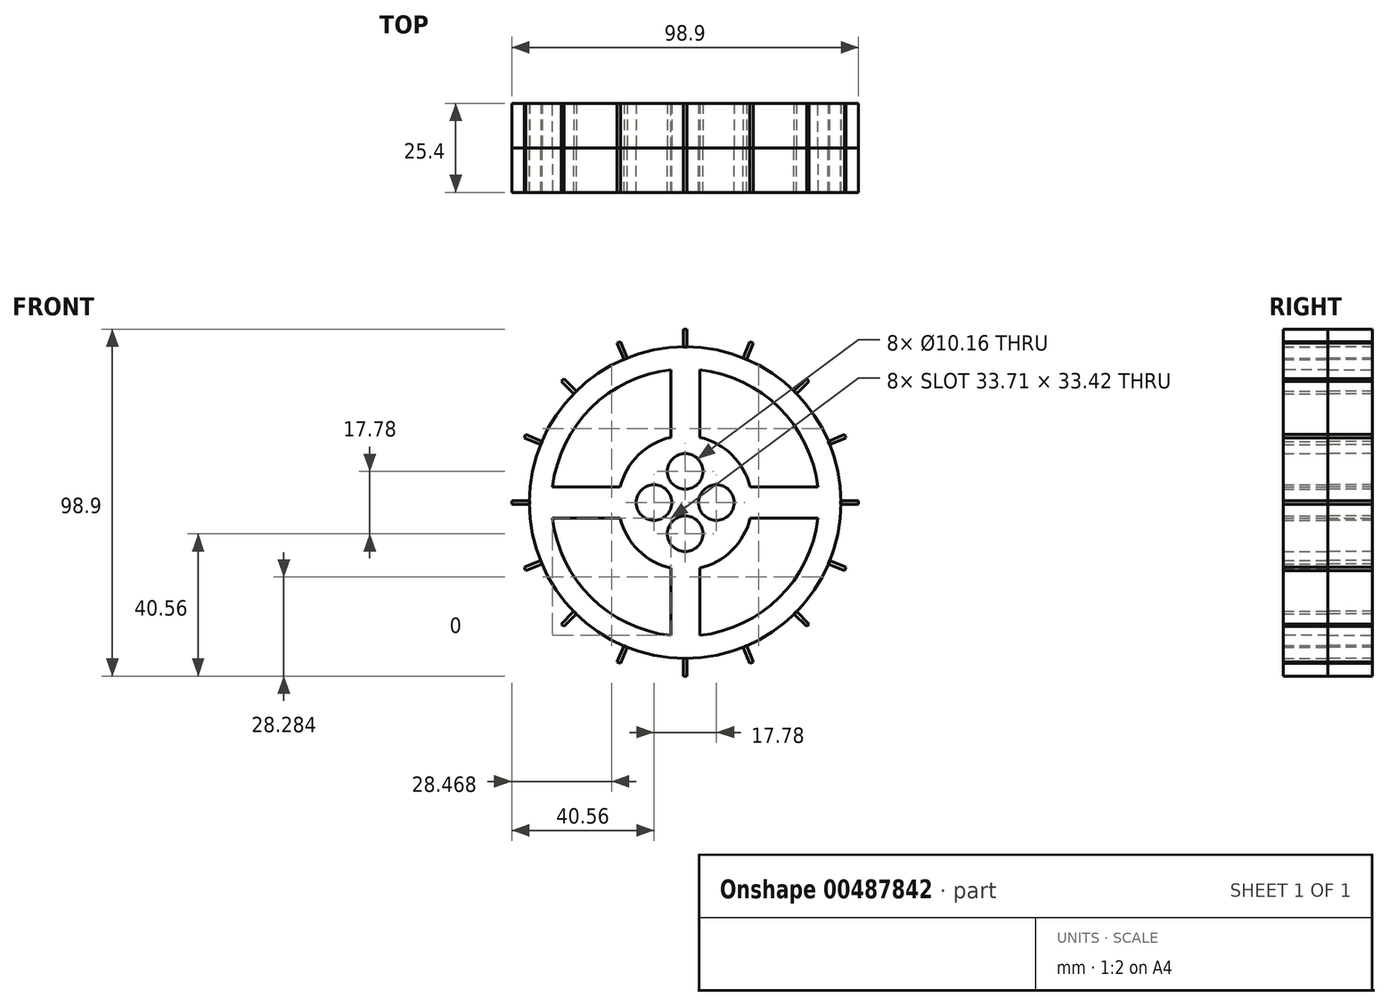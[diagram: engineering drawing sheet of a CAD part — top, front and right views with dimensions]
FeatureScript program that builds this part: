
annotation { "Feature Type Name" : "Feature", "Feature Type Description" : "" }
export const myFeature = defineFeature(function(context is Context, id is Id, definition is map)
    precondition{}
    {
        {
            var Q0;
            Q0=qCreatedBy(makeId("Front.planeOp"),FACE);
            var sketch = newSketch(context, id + "F0", { "sketchPlane" : qUnion([Q0])});
            skCircle(sketch, "E0", {"center": v(0, 0) * mm, "radius": 44.45 * mm});
            skSolve(sketch);
        }
        {
            var Q0;
            Q0=makeQuery(id+"F0.imprint","IMPRINT",FACE,{"disambiguationData":[TD([[makeQuery(id+"F0.imprint","IMPRINT",EDGE,{"derivedFrom":sQuery(id+"F0.wireOp",EDGE,"E0")}),1.0]])]});
            extrude(context, id + "F1", {"entities" : qUnion([Q0]), "depth" : 12.7 * mm});
        }
        {
            var Q0;
            Q0=makeQuery(id+"F1.opExtrude","CAP_FACE",FACE,{"disambiguationData":[OSD([sQuery(id+"F0.wireOp",EDGE,"E0")])],"isStart":false});
            var sketch = newSketch(context, id + "F2", { "sketchPlane" : qUnion([Q0])});
            skCircle(sketch, "E1", {"center": v(0, 0) * mm, "radius": 50.8 * mm});
            skSolve(sketch);
        }
        {
            var Q0;
            Q0=sQuery(id+"F2.wireOp",VERTEX,"E1.center");
            var Q1;
            Q1=makeQuery(id+"F1.opExtrude","SWEPT_BODY",BODY,{"disambiguationData":[OSD([sQuery(id+"F0.wireOp",EDGE,"E0")])]});
            hole(context, id + "F3", {"style" : HoleStyle.SIMPLE, "endStyle" : HoleEndStyle.THROUGH, "holeDiameter" : 76.2 * mm, "isTappedThrough" : true, "tappedDepth" : 12.7 * mm, "tapClearance" : 3, "locations" : qUnion([Q0]), "scope" : qUnion([Q1])});
        }
        {
            var Q0;
            Q0=qCreatedBy(makeId("Front.planeOp"),FACE);
            var sketch = newSketch(context, id + "F4", { "sketchPlane" : qUnion([Q0])});
            skLineSegment(sketch, "E2.bottom", {"start": v(4.13, -42.15) * mm, "end": v(-4.13, -42.15) * mm});
            skLineSegment(sketch, "E2.top", {"start": v(4.13, 42.15) * mm, "end": v(-4.13, 42.15) * mm});
            skLineSegment(sketch, "E2.left", {"start": v(4.13, -42.15) * mm, "end": v(4.13, 42.15) * mm});
            skLineSegment(sketch, "E2.right", {"start": v(-4.13, -42.15) * mm, "end": v(-4.13, 42.15) * mm});
            skPoint(sketch, "E2.middle", {"position": v(0, 0) * mm});
            skLineSegment(sketch, "E3.bottom", {"start": v(42.66, 4.46) * mm, "end": v(-42.66, 4.46) * mm});
            skLineSegment(sketch, "E3.top", {"start": v(42.66, -4.46) * mm, "end": v(-42.66, -4.46) * mm});
            skLineSegment(sketch, "E3.left", {"start": v(42.66, 4.46) * mm, "end": v(42.66, -4.46) * mm});
            skLineSegment(sketch, "E3.right", {"start": v(-42.66, 4.46) * mm, "end": v(-42.66, -4.46) * mm});
            skSolve(sketch);
        }
        {
            var Q0;
            {var subQ5=sQuery(id+"F4.wireOp",EDGE,"E3.left");Q0=makeQuery(id+"F4.imprint","IMPRINT",FACE,{"disambiguationData":[TD([[makeQuery(id+"F4.imprint","IMPRINT",EDGE,{"derivedFrom":subQ5}),-1.0]])]});}
            var Q1;
            {var subQ5=sQuery(id+"F4.wireOp",EDGE,"E3.right");Q1=makeQuery(id+"F4.imprint","IMPRINT",FACE,{"disambiguationData":[TD([[makeQuery(id+"F4.imprint","IMPRINT",EDGE,{"derivedFrom":subQ5}),1.0]])]});}
            var Q2;
            {var subQ0=sQuery(id+"F4.wireOp",EDGE,"E3.top");var subQ1=sQuery(id+"F4.wireOp",EDGE,"E2.left");var subQ2=makeQuery(id+"F4.imprint","INTERSECT",VERTEX,{"derivedFrom":[subQ1,subQ0]});Q2=makeQuery(id+"F4.imprint","IMPRINT",FACE,{"disambiguationData":[TD([[makeQuery(id+"F4.imprint","IMPRINT",EDGE,{"disambiguationData":[TD([[subQ2,-1.0]])],"derivedFrom":subQ1}),1.0]])]});}
            var Q3;
            {var subQ0=sQuery(id+"F4.wireOp",EDGE,"E2.top");Q3=makeQuery(id+"F4.imprint","IMPRINT",FACE,{"disambiguationData":[TD([[makeQuery(id+"F4.imprint","IMPRINT",EDGE,{"derivedFrom":subQ0}),1.0]])]});}
            var Q4;
            {var subQ0=sQuery(id+"F4.wireOp",EDGE,"E2.bottom");Q4=makeQuery(id+"F4.imprint","IMPRINT",FACE,{"disambiguationData":[TD([[makeQuery(id+"F4.imprint","IMPRINT",EDGE,{"derivedFrom":subQ0}),-1.0]])]});}
            extrude(context, id + "F5", {"entities" : qUnion([Q0, Q1, Q2, Q3, Q4]), "operationType" : NewBodyOperationType.ADD, "depth" : 12.7 * mm});
        }
        {
            var Q0;
            Q0=qCreatedBy(makeId("Front.planeOp"),FACE);
            var sketch = newSketch(context, id + "F6", { "sketchPlane" : qUnion([Q0])});
            skCircle(sketch, "E4", {"center": v(0, 0) * mm, "radius": 19.05 * mm});
            skSolve(sketch);
        }
        {
            var Q0;
            Q0=makeQuery(id+"F6.imprint","IMPRINT",FACE,{"disambiguationData":[TD([[makeQuery(id+"F6.imprint","IMPRINT",EDGE,{"derivedFrom":sQuery(id+"F6.wireOp",EDGE,"E4")}),1.0]])]});
            extrude(context, id + "F7", {"entities" : qUnion([Q0]), "operationType" : NewBodyOperationType.ADD, "depth" : 12.7 * mm});
        }
        {
            var Q0;
            Q0=qCreatedBy(makeId("Front.planeOp"),FACE);
            var sketch = newSketch(context, id + "F8", { "sketchPlane" : qUnion([Q0])});
            skCircle(sketch, "E5", {"center": v(0, 8.9) * mm, "radius": 5.08 * mm});
            skCircle(sketch, "E6", {"center": v(8.9, 0) * mm, "radius": 5.08 * mm});
            skCircle(sketch, "E7", {"center": v(0, -8.9) * mm, "radius": 5.08 * mm});
            skCircle(sketch, "E8", {"center": v(-8.9, 0) * mm, "radius": 5.08 * mm});
            skSolve(sketch);
        }
        {
            var Q0;
            Q0=qSketchRegion(id+"F8",true);
            extrude(context, id + "F9", {"entities" : qUnion([Q0]), "operationType" : NewBodyOperationType.REMOVE, "endBound" : BoundingType.THROUGH_ALL, "depth" : 25.4 * mm});
        }
        {
            var Q0;
            Q0=qCreatedBy(makeId("Front.planeOp"),FACE);
            var sketch = newSketch(context, id + "F10", { "sketchPlane" : qUnion([Q0])});
            skLineSegment(sketch, "E9.bottom", {"start": v(-0.52, 49.45) * mm, "end": v(0.52, 49.45) * mm});
            skLineSegment(sketch, "E9.top", {"start": v(-0.52, 44.37) * mm, "end": v(0.52, 44.37) * mm});
            skLineSegment(sketch, "E9.left", {"start": v(-0.52, 49.45) * mm, "end": v(-0.52, 44.37) * mm});
            skLineSegment(sketch, "E9.right", {"start": v(0.52, 49.45) * mm, "end": v(0.52, 44.37) * mm});
            skPoint(sketch, "E9.middle", {"position": v(0, 46.9) * mm});
            skSolve(sketch);
        }
        {
            var Q0;
            Q0=makeQuery(id+"F10.imprint","IMPRINT",FACE,{"disambiguationData":[TD([[makeQuery(id+"F10.imprint","IMPRINT",EDGE,{"derivedFrom":sQuery(id+"F10.wireOp",EDGE,"E9.bottom")}),-1.0]])]});
            extrude(context, id + "F11", {"entities" : qUnion([Q0]), "depth" : 12.7 * mm});
        }
        {
            var Q0;
            Q0=makeQuery(id+"F11.opExtrude","SWEPT_BODY",BODY,{"disambiguationData":[OSD([sQuery(id+"F10.wireOp",EDGE,"E9.bottom"),sQuery(id+"F10.wireOp",EDGE,"E9.top"),sQuery(id+"F10.wireOp",EDGE,"E9.left"),sQuery(id+"F10.wireOp",EDGE,"E9.right")])]});
            var Q1;
            {var subQ0=makeQuery(id+"F1.opExtrude","SWEPT_FACE",FACE,{"disambiguationData":[OSD([sQuery(id+"F0.wireOp",EDGE,"E0")])]});Q1=makeQuery(id+"FaYJ1gs6lbwXeL1_1.boolean.opBoolean","MERGE",FACE,{"derivedFrom":[subQ0,makeQuery(id+"FaYJ1gs6lbwXeL1_1.opPattern","COPY",FACE,{"derivedFrom":subQ0,"instanceName":"1"})]});}
            circularPattern(context, id + "F12", {"entities" : qUnion([Q0]), "axis" : qUnion([Q1]), "angle" : 360 * degree, "instanceCount" : 16, "equalSpace" : true});
        }
        {
            var Q0;
            Q0=makeQuery(id+"F12.opPattern","COPY",BODY,{"derivedFrom":makeQuery(id+"F11.opExtrude","SWEPT_BODY",BODY,{"disambiguationData":[OSD([sQuery(id+"F10.wireOp",EDGE,"E9.bottom"),sQuery(id+"F10.wireOp",EDGE,"E9.top"),sQuery(id+"F10.wireOp",EDGE,"E9.left"),sQuery(id+"F10.wireOp",EDGE,"E9.right")])]}),"instanceName":"15"});
            var Q1;
            Q1=makeQuery(id+"F12.opPattern","COPY",BODY,{"derivedFrom":makeQuery(id+"F11.opExtrude","SWEPT_BODY",BODY,{"disambiguationData":[OSD([sQuery(id+"F10.wireOp",EDGE,"E9.bottom"),sQuery(id+"F10.wireOp",EDGE,"E9.top"),sQuery(id+"F10.wireOp",EDGE,"E9.left"),sQuery(id+"F10.wireOp",EDGE,"E9.right")])]}),"instanceName":"14"});
            var Q2;
            Q2=makeQuery(id+"F12.opPattern","COPY",BODY,{"derivedFrom":makeQuery(id+"F11.opExtrude","SWEPT_BODY",BODY,{"disambiguationData":[OSD([sQuery(id+"F10.wireOp",EDGE,"E9.bottom"),sQuery(id+"F10.wireOp",EDGE,"E9.top"),sQuery(id+"F10.wireOp",EDGE,"E9.left"),sQuery(id+"F10.wireOp",EDGE,"E9.right")])]}),"instanceName":"13"});
            var Q3;
            Q3=makeQuery(id+"F12.opPattern","COPY",BODY,{"derivedFrom":makeQuery(id+"F11.opExtrude","SWEPT_BODY",BODY,{"disambiguationData":[OSD([sQuery(id+"F10.wireOp",EDGE,"E9.bottom"),sQuery(id+"F10.wireOp",EDGE,"E9.top"),sQuery(id+"F10.wireOp",EDGE,"E9.left"),sQuery(id+"F10.wireOp",EDGE,"E9.right")])]}),"instanceName":"12"});
            var Q4;
            Q4=makeQuery(id+"F12.opPattern","COPY",BODY,{"derivedFrom":makeQuery(id+"F11.opExtrude","SWEPT_BODY",BODY,{"disambiguationData":[OSD([sQuery(id+"F10.wireOp",EDGE,"E9.bottom"),sQuery(id+"F10.wireOp",EDGE,"E9.top"),sQuery(id+"F10.wireOp",EDGE,"E9.left"),sQuery(id+"F10.wireOp",EDGE,"E9.right")])]}),"instanceName":"11"});
            var Q5;
            Q5=makeQuery(id+"F12.opPattern","COPY",BODY,{"derivedFrom":makeQuery(id+"F11.opExtrude","SWEPT_BODY",BODY,{"disambiguationData":[OSD([sQuery(id+"F10.wireOp",EDGE,"E9.bottom"),sQuery(id+"F10.wireOp",EDGE,"E9.top"),sQuery(id+"F10.wireOp",EDGE,"E9.left"),sQuery(id+"F10.wireOp",EDGE,"E9.right")])]}),"instanceName":"10"});
            var Q6;
            Q6=makeQuery(id+"F12.opPattern","COPY",BODY,{"derivedFrom":makeQuery(id+"F11.opExtrude","SWEPT_BODY",BODY,{"disambiguationData":[OSD([sQuery(id+"F10.wireOp",EDGE,"E9.bottom"),sQuery(id+"F10.wireOp",EDGE,"E9.top"),sQuery(id+"F10.wireOp",EDGE,"E9.left"),sQuery(id+"F10.wireOp",EDGE,"E9.right")])]}),"instanceName":"9"});
            var Q7;
            Q7=makeQuery(id+"F12.opPattern","COPY",BODY,{"derivedFrom":makeQuery(id+"F11.opExtrude","SWEPT_BODY",BODY,{"disambiguationData":[OSD([sQuery(id+"F10.wireOp",EDGE,"E9.bottom"),sQuery(id+"F10.wireOp",EDGE,"E9.top"),sQuery(id+"F10.wireOp",EDGE,"E9.left"),sQuery(id+"F10.wireOp",EDGE,"E9.right")])]}),"instanceName":"8"});
            var Q8;
            Q8=makeQuery(id+"F12.opPattern","COPY",BODY,{"derivedFrom":makeQuery(id+"F11.opExtrude","SWEPT_BODY",BODY,{"disambiguationData":[OSD([sQuery(id+"F10.wireOp",EDGE,"E9.bottom"),sQuery(id+"F10.wireOp",EDGE,"E9.top"),sQuery(id+"F10.wireOp",EDGE,"E9.left"),sQuery(id+"F10.wireOp",EDGE,"E9.right")])]}),"instanceName":"7"});
            var Q9;
            Q9=makeQuery(id+"F12.opPattern","COPY",BODY,{"derivedFrom":makeQuery(id+"F11.opExtrude","SWEPT_BODY",BODY,{"disambiguationData":[OSD([sQuery(id+"F10.wireOp",EDGE,"E9.bottom"),sQuery(id+"F10.wireOp",EDGE,"E9.top"),sQuery(id+"F10.wireOp",EDGE,"E9.left"),sQuery(id+"F10.wireOp",EDGE,"E9.right")])]}),"instanceName":"6"});
            var Q10;
            Q10=makeQuery(id+"F12.opPattern","COPY",BODY,{"derivedFrom":makeQuery(id+"F11.opExtrude","SWEPT_BODY",BODY,{"disambiguationData":[OSD([sQuery(id+"F10.wireOp",EDGE,"E9.bottom"),sQuery(id+"F10.wireOp",EDGE,"E9.top"),sQuery(id+"F10.wireOp",EDGE,"E9.left"),sQuery(id+"F10.wireOp",EDGE,"E9.right")])]}),"instanceName":"5"});
            var Q11;
            Q11=makeQuery(id+"F12.opPattern","COPY",BODY,{"derivedFrom":makeQuery(id+"F11.opExtrude","SWEPT_BODY",BODY,{"disambiguationData":[OSD([sQuery(id+"F10.wireOp",EDGE,"E9.bottom"),sQuery(id+"F10.wireOp",EDGE,"E9.top"),sQuery(id+"F10.wireOp",EDGE,"E9.left"),sQuery(id+"F10.wireOp",EDGE,"E9.right")])]}),"instanceName":"4"});
            var Q12;
            Q12=makeQuery(id+"F12.opPattern","COPY",BODY,{"derivedFrom":makeQuery(id+"F11.opExtrude","SWEPT_BODY",BODY,{"disambiguationData":[OSD([sQuery(id+"F10.wireOp",EDGE,"E9.bottom"),sQuery(id+"F10.wireOp",EDGE,"E9.top"),sQuery(id+"F10.wireOp",EDGE,"E9.left"),sQuery(id+"F10.wireOp",EDGE,"E9.right")])]}),"instanceName":"3"});
            var Q13;
            Q13=makeQuery(id+"F12.opPattern","COPY",BODY,{"derivedFrom":makeQuery(id+"F11.opExtrude","SWEPT_BODY",BODY,{"disambiguationData":[OSD([sQuery(id+"F10.wireOp",EDGE,"E9.bottom"),sQuery(id+"F10.wireOp",EDGE,"E9.top"),sQuery(id+"F10.wireOp",EDGE,"E9.left"),sQuery(id+"F10.wireOp",EDGE,"E9.right")])]}),"instanceName":"2"});
            var Q14;
            Q14=makeQuery(id+"F12.opPattern","COPY",BODY,{"derivedFrom":makeQuery(id+"F11.opExtrude","SWEPT_BODY",BODY,{"disambiguationData":[OSD([sQuery(id+"F10.wireOp",EDGE,"E9.bottom"),sQuery(id+"F10.wireOp",EDGE,"E9.top"),sQuery(id+"F10.wireOp",EDGE,"E9.left"),sQuery(id+"F10.wireOp",EDGE,"E9.right")])]}),"instanceName":"1"});
            var Q15;
            Q15=makeQuery(id+"F11.opExtrude","SWEPT_BODY",BODY,{"disambiguationData":[OSD([sQuery(id+"F10.wireOp",EDGE,"E9.bottom"),sQuery(id+"F10.wireOp",EDGE,"E9.top"),sQuery(id+"F10.wireOp",EDGE,"E9.left"),sQuery(id+"F10.wireOp",EDGE,"E9.right")])]});
            var Q16;
            Q16=makeQuery(id+"F1.opExtrude","SWEPT_BODY",BODY,{"disambiguationData":[OSD([sQuery(id+"F0.wireOp",EDGE,"E0")])]});
            var Q17;
            Q17=qCreatedBy(makeId("Front.planeOp"),FACE);
            mirror(context, id + "F13", {"entities" : qUnion([Q0, Q1, Q2, Q3, Q4, Q5, Q6, Q7, Q8, Q9, Q10, Q11, Q12, Q13, Q14, Q15, Q16]), "mirrorPlane" : qUnion([Q17])});
        }
    });
